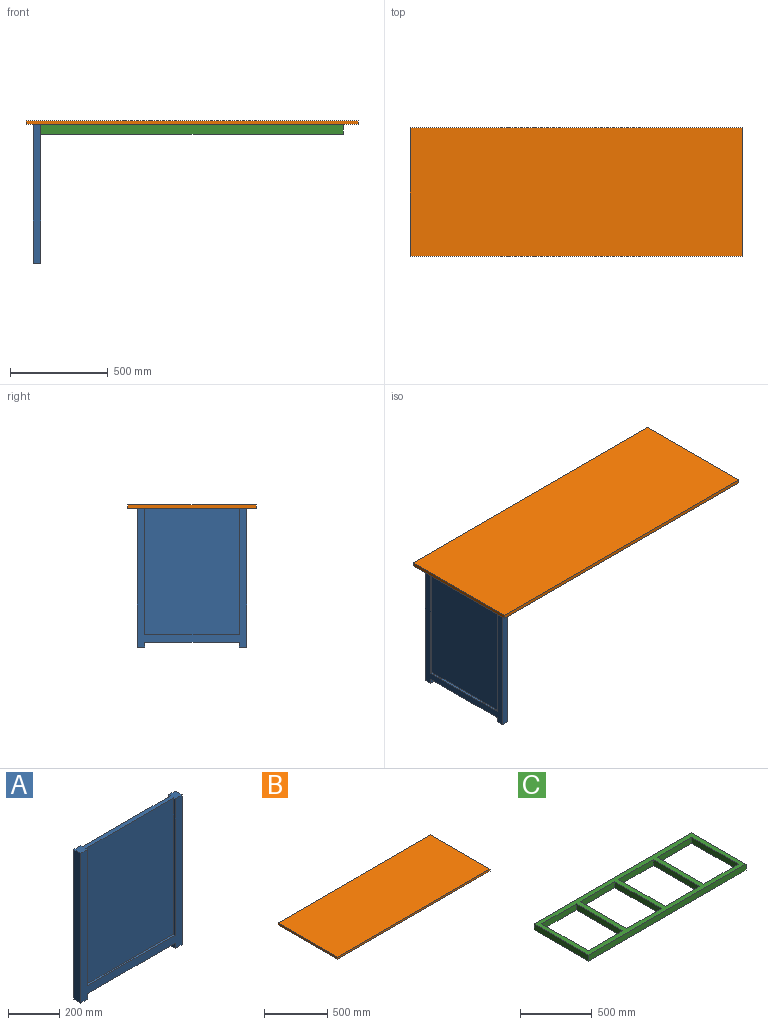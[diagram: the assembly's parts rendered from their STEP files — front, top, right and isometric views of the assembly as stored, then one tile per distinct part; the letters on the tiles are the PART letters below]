
ASSEMBLY  parts=3 mates=3
PART A: 18 faces, bbox 558.8x38.1x711.2 mm
  f0: plane 647.7x9.53mm, normal (1,0,0), area 6169.3mm2, adj f5,f9,f15,f16
  f1: plane 647.7x9.53mm, normal (-1,0,0), area 6169.3mm2, adj f5,f9,f15,f16
  f2: plane 482.6x9.53mm, normal (0,0,1), area 4596.8mm2, adj f3,f7,f10,f17
  f3: plane 647.7x9.53mm, normal (1,0,0), area 6169.3mm2, adj f2,f7,f9,f17
  f4: plane 711.2x38.1mm, normal (-1,0,0), area 27096.7mm2, adj f5,f7,f8,f9
  f5: plane 711.2x558.8mm, normal (0,-1,0), area 72580.5mm2, adj f0,f1,f4,f6,f8,f9,f11,f12
  f6: plane 38.1x25.4mm, normal (1,0,0), area 967.7mm2, adj f5,f7,f8,f14
  f7: plane 711.2x558.8mm, normal (0,1,0), area 72580.5mm2, adj f2,f3,f4,f6,f8,f9,f10,f11
  f8: plane 38.1x38.1mm, normal (0,0,-1), area 1451.6mm2, adj f4,f5,f6,f7
  f9: plane 558.8x38.1mm, normal (0,0,1), area 12096.7mm2, adj f0,f1,f3,f4,f5,f7,f10,f11
  f10: plane 647.7x9.53mm, normal (-1,0,0), area 6169.3mm2, adj f2,f7,f9,f17
  f11: plane 711.2x38.1mm, normal (1,0,0), area 27096.7mm2, adj f5,f7,f9,f13
  f12: plane 38.1x25.4mm, normal (-1,0,0), area 967.7mm2, adj f5,f7,f13,f14
  f13: plane 38.1x38.1mm, normal (0,0,-1), area 1451.6mm2, adj f5,f7,f11,f12
  f14: plane 482.6x38.1mm, normal (0,0,-1), area 18387.1mm2, adj f5,f6,f7,f12
  f15: plane 482.6x9.53mm, normal (0,0,1), area 4596.8mm2, adj f0,f1,f5,f16
  f16: plane 647.7x482.6mm, normal (0,-1,0), area 312580mm2, adj f0,f1,f9,f15
  f17: plane 647.7x482.6mm, normal (0,1,0), area 312580mm2, adj f2,f3,f9,f10
PART B: 6 faces, bbox 1701.8x660.4x19.1 mm
  f0: plane 660.4x19.05mm, normal (-1,0,0), area 12580.6mm2, adj f1,f3,f4,f5
  f1: plane 1701.8x19.05mm, normal (0,-1,0), area 32419.3mm2, adj f0,f2,f4,f5
  f2: plane 660.4x19.05mm, normal (1,0,0), area 12580.6mm2, adj f1,f3,f4,f5
  f3: plane 1701.8x19.05mm, normal (0,1,0), area 32419.3mm2, adj f0,f2,f4,f5
  f4: plane 1701.8x660.4mm, normal (0,0,1), area 1123868.7mm2, adj f0,f1,f2,f3
  f5: plane 1701.8x660.4mm, normal (0,0,-1), area 1123868.7mm2, adj f0,f1,f2,f3
PART C: 22 faces, bbox 1549.4x533.4x50.8 mm
  f0: plane 339.73x50.8mm, normal (0,1,0), area 17258mm2, adj f7,f8,f15,f21
  f1: plane 339.73x50.8mm, normal (0,1,0), area 17258mm2, adj f7,f8,f14,f17
  f2: plane 339.73x50.8mm, normal (0,1,0), area 17258mm2, adj f7,f8,f16,f19
  f3: plane 339.73x50.8mm, normal (0,1,0), area 17258mm2, adj f7,f8,f18,f20
  f4: plane 533.4x50.8mm, normal (-1,0,0), area 27096.7mm2, adj f5,f7,f8,f13
  f5: plane 1549.4x50.8mm, normal (0,-1,0), area 78709.5mm2, adj f4,f6,f7,f8
  f6: plane 533.4x50.8mm, normal (1,0,0), area 27096.7mm2, adj f5,f7,f8,f13
  f7: plane 1549.4x533.4mm, normal (0,0,1), area 205160.9mm2, adj f0,f1,f2,f3,f4,f5,f6,f9
  f8: plane 1549.4x533.4mm, normal (0,0,-1), area 205160.9mm2, adj f0,f1,f2,f3,f4,f5,f6,f9
  f9: plane 339.73x50.8mm, normal (0,-1,0), area 17258mm2, adj f7,f8,f18,f20
  f10: plane 339.73x50.8mm, normal (0,-1,0), area 17258mm2, adj f7,f8,f16,f19
  f11: plane 339.73x50.8mm, normal (0,-1,0), area 17258mm2, adj f7,f8,f14,f17
  f12: plane 339.73x50.8mm, normal (0,-1,0), area 17258mm2, adj f7,f8,f15,f21
  f13: plane 1549.4x50.8mm, normal (0,1,0), area 78709.5mm2, adj f4,f6,f7,f8
  f14: plane 457.2x50.8mm, normal (1,0,0), area 23225.8mm2, adj f1,f7,f8,f11
  f15: plane 457.2x50.8mm, normal (-1,0,0), area 23225.8mm2, adj f0,f7,f8,f12
  f16: plane 457.2x50.8mm, normal (1,0,0), area 23225.8mm2, adj f2,f7,f8,f10
  f17: plane 457.2x50.8mm, normal (-1,0,0), area 23225.8mm2, adj f1,f7,f8,f11
  f18: plane 457.2x50.8mm, normal (1,0,0), area 23225.8mm2, adj f3,f7,f8,f9
  f19: plane 457.2x50.8mm, normal (-1,0,0), area 23225.8mm2, adj f2,f7,f8,f10
  f20: plane 457.2x50.8mm, normal (-1,0,0), area 23225.8mm2, adj f3,f7,f8,f9
  f21: plane 457.2x50.8mm, normal (1,0,0), area 23225.8mm2, adj f0,f7,f8,f12
PLACE A rot(axis=(0,0,-1),90deg) t=(-793.75,0,0)mm
PLACE B at identity
PLACE C t=(0,12.7,-50.8)mm
MATE fastened C.f7 <-> B.f5  axis (0,0,1) through (0,0,0)mm
MATE planar A.f7 <-> C.f4  axis (1,0,0) through (-774.7,0,-434.42)mm
MATE planar A.f9 <-> B.f5  axis (0,0,1) through (-793.75,0,0)mm
